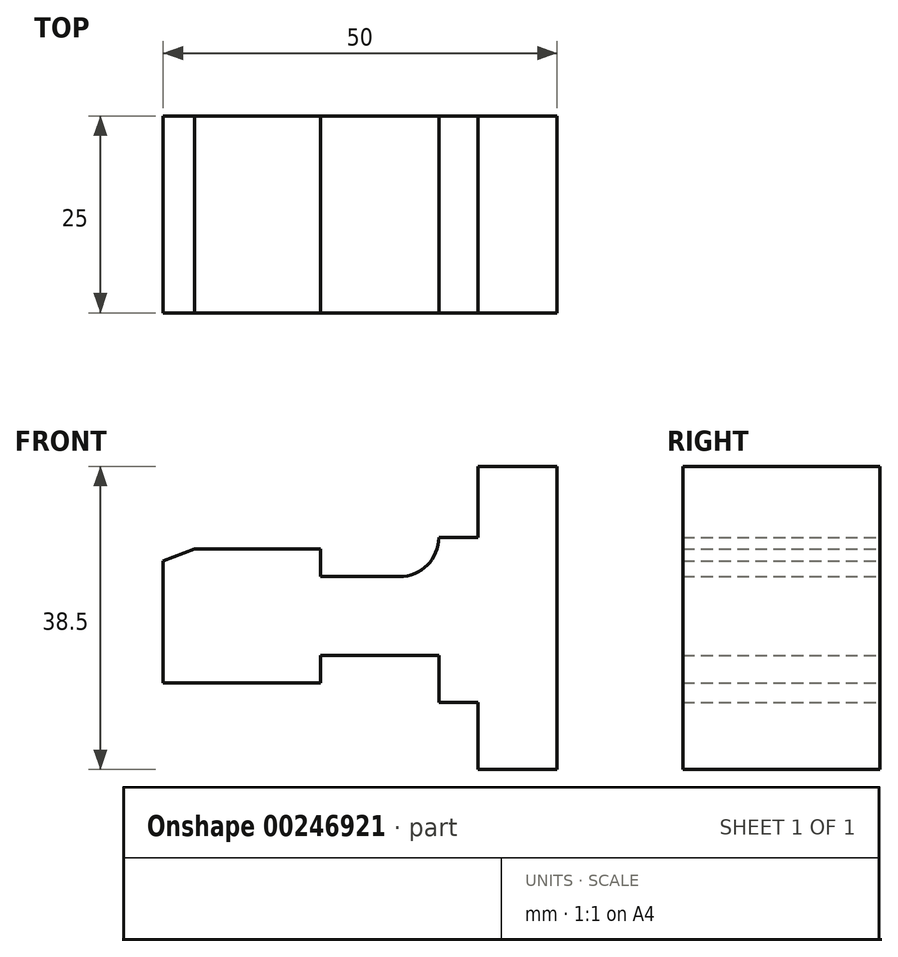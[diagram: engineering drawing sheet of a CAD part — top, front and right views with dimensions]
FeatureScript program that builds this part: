
annotation { "Feature Type Name" : "Feature", "Feature Type Description" : "" }
export const myFeature = defineFeature(function(context is Context, id is Id, definition is map)
    precondition{}
    {
        {
            var Q0;
            Q0=qCreatedBy(makeId("Front.planeOp"),FACE);
            var sketch = newSketch(context, id + "F0", { "sketchPlane" : qUnion([Q0])});
            skLineSegment(sketch, "E0", {"start": v(-29.25, 0) * mm, "end": v(29.14, 0) * mm, "construction": true});
            skLineSegment(sketch, "E1", {"start": v(-24.27, -8.5) * mm, "end": v(-24.27, 6.96) * mm});
            skLineSegment(sketch, "E2", {"start": v(-24.27, 6.96) * mm, "end": v(-20.27, 8.5) * mm});
            skLineSegment(sketch, "E3", {"start": v(-20.27, 8.5) * mm, "end": v(-4.27, 8.5) * mm});
            skLineSegment(sketch, "E4", {"start": v(-4.27, 8.5) * mm, "end": v(-4.27, 5) * mm});
            skLineSegment(sketch, "E5", {"start": v(-4.27, 5) * mm, "end": v(5.73, 5) * mm});
            skLineSegment(sketch, "E6", {"start": v(10.73, 10) * mm, "end": v(10.73, 10) * mm});
            skLineSegment(sketch, "E7", {"start": v(10.73, 10) * mm, "end": v(15.73, 10) * mm});
            skLineSegment(sketch, "E8", {"start": v(15.73, 10) * mm, "end": v(15.73, 19) * mm});
            skLineSegment(sketch, "E9", {"start": v(15.73, 19) * mm, "end": v(25.73, 19) * mm});
            skLineSegment(sketch, "E10", {"start": v(25.73, 19) * mm, "end": v(25.73, -19.5) * mm});
            skLineSegment(sketch, "E11", {"start": v(25.73, -19.5) * mm, "end": v(15.73, -19.5) * mm});
            skLineSegment(sketch, "E12", {"start": v(15.73, -19.5) * mm, "end": v(15.73, -11) * mm});
            skLineSegment(sketch, "E13", {"start": v(15.73, -11) * mm, "end": v(10.73, -11) * mm});
            skLineSegment(sketch, "E14", {"start": v(10.73, -11) * mm, "end": v(10.73, -5) * mm});
            skLineSegment(sketch, "E15", {"start": v(10.73, -5) * mm, "end": v(-4.27, -5) * mm});
            skLineSegment(sketch, "E16", {"start": v(-4.27, -5) * mm, "end": v(-4.27, -8.5) * mm});
            skLineSegment(sketch, "E17", {"start": v(-4.27, -8.5) * mm, "end": v(-24.27, -8.5) * mm});
            skPoint(sketch, "E18.visualSharp", {"position": v(10.73, 5) * mm});
            skArc(sketch, "E18.filletArc", {"start": v(5.73, 5) * mm, "mid": v(9.26, 6.46) * mm, "end": v(10.73, 10) * mm});
            skSolve(sketch);
        }
        {
            var Q0;
            Q0 = qSketchRegion(id + "F0", true);
            extrude(context, id + "F1", {"entities" : qUnion([Q0]), "depth" : 25 * mm});
        }
    });
